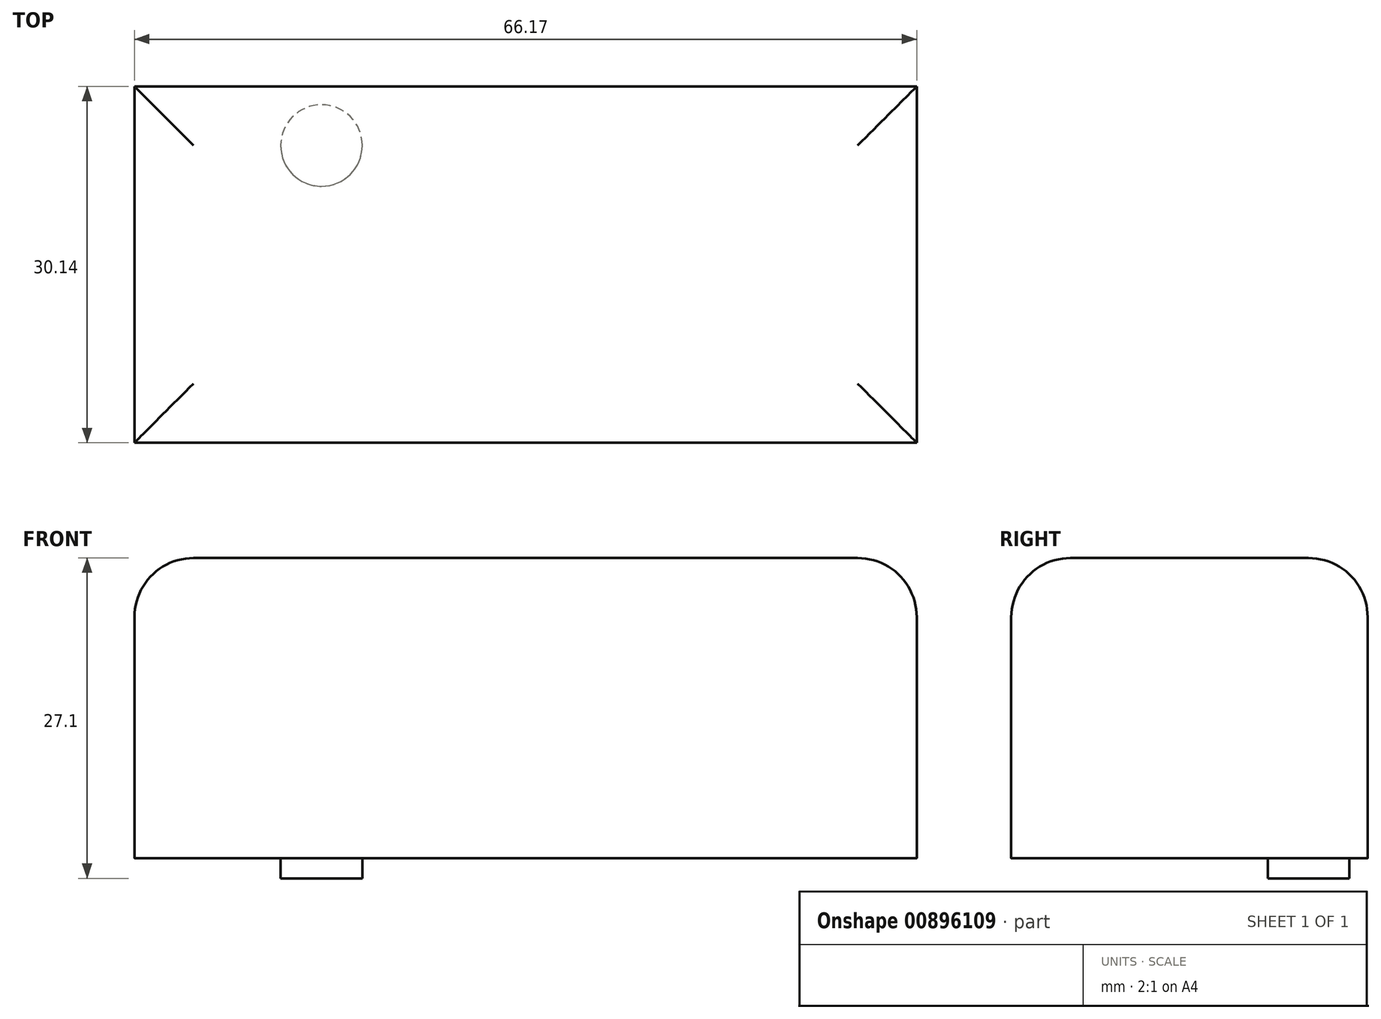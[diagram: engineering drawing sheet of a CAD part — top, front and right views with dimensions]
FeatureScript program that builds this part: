
annotation { "Feature Type Name" : "Feature", "Feature Type Description" : "" }
export const myFeature = defineFeature(function(context is Context, id is Id, definition is map)
    precondition{}
    {
        {
            var Q0;
            Q0=qCreatedBy(makeId("Top.planeOp"),FACE);
            var sketch = newSketch(context, id + "F0", { "sketchPlane" : qUnion([Q0])});
            skLineSegment(sketch, "E0.bottom", {"start": v(-31.19, 11.28) * mm, "end": v(34.98, 11.28) * mm});
            skLineSegment(sketch, "E0.top", {"start": v(-31.19, -18.86) * mm, "end": v(34.98, -18.86) * mm});
            skLineSegment(sketch, "E0.left", {"start": v(-31.19, 11.28) * mm, "end": v(-31.19, -18.86) * mm});
            skLineSegment(sketch, "E0.right", {"start": v(34.98, 11.28) * mm, "end": v(34.98, -18.86) * mm});
            skSolve(sketch);
        }
        {
            var Q0;
            Q0=makeQuery(id+"F0.imprint","IMPRINT",FACE,{"disambiguationData":[TD([[makeQuery(id+"F0.imprint","IMPRINT",EDGE,{"derivedFrom":sQuery(id+"F0.wireOp",EDGE,"E0.bottom")}),-1.0]])]});
            extrude(context, id + "F1", {"entities" : qUnion([Q0]), "depth" : 25.4 * mm, "offsetDistance" : 25.4 * mm});
        }
        {
            var Q0;
            Q0=qCreatedBy(makeId("Top.planeOp"),FACE);
            var sketch = newSketch(context, id + "F2", { "sketchPlane" : qUnion([Q0])});
            skCircle(sketch, "E1", {"center": v(21, -4.39) * mm, "radius": 10.1 * mm});
            skSolve(sketch);
        }
        {
            var Q0;
            Q0=sQuery(id+"F2.wireOp",EDGE,"E1");
            extrude(context, id + "F3", {"bodyType" : ToolBodyType.SURFACE, "surfaceEntities" : qUnion([Q0]), "depth" : 42.8 * mm, "offsetDistance" : 25 * mm});
        }
        {
            var Q0;
            Q0=makeQuery(id+"F1.opExtrude","SWEPT_FACE",FACE,{"disambiguationData":[OSD([sQuery(id+"F0.wireOp",EDGE,"E0.bottom")])]});
            var sketch = newSketch(context, id + "F4", { "sketchPlane" : qUnion([Q0])});
            skCircle(sketch, "E2", {"center": v(21.23, 13.84) * mm, "radius": 4.22 * mm});
            skSolve(sketch);
        }
        {
            var Q0;
            Q0=sQuery(id+"F4.wireOp",EDGE,"E2");
            extrude(context, id + "F5", {"bodyType" : ToolBodyType.SURFACE, "surfaceEntities" : qUnion([Q0]), "depth" : 3.1 * mm, "offsetDistance" : 25 * mm});
        }
        {
            var Q0;
            Q0=makeQuery(id+"F1.opExtrude","CAP_FACE",FACE,{"disambiguationData":[OSD([sQuery(id+"F0.wireOp",EDGE,"E0.bottom"),sQuery(id+"F0.wireOp",EDGE,"E0.top"),sQuery(id+"F0.wireOp",EDGE,"E0.left"),sQuery(id+"F0.wireOp",EDGE,"E0.right")])],"isStart":true});
            var sketch = newSketch(context, id + "F6", { "sketchPlane" : qUnion([Q0])});
            skCircle(sketch, "E3", {"center": v(-15.36, -6.28) * mm, "radius": 3.45 * mm});
            skSolve(sketch);
        }
        {
            var Q0;
            Q0 = qSketchRegion(id + "F6", true);
            extrude(context, id + "F7", {"entities" : qUnion([Q0]), "operationType" : NewBodyOperationType.ADD, "depth" : 1.7 * mm, "offsetDistance" : 25 * mm});
        }
        {
            var Q0;
            Q0=makeQuery(id+"F1.opExtrude","CAP_FACE",FACE,{"disambiguationData":[OSD([sQuery(id+"F0.wireOp",EDGE,"E0.bottom"),sQuery(id+"F0.wireOp",EDGE,"E0.top"),sQuery(id+"F0.wireOp",EDGE,"E0.left"),sQuery(id+"F0.wireOp",EDGE,"E0.right")])],"isStart":false});
            fillet(context, id + "F8", {"entities" : qUnion([Q0]), "radius" : 5 * mm, "tangentPropagation" : true, "allowEdgeOverflow" : false});
        }
        {
            var Q0;
            Q0=makeQuery(id+"F1.opExtrude","CAP_FACE",FACE,{"disambiguationData":[OSD([sQuery(id+"F0.wireOp",EDGE,"E0.bottom"),sQuery(id+"F0.wireOp",EDGE,"E0.top"),sQuery(id+"F0.wireOp",EDGE,"E0.left"),sQuery(id+"F0.wireOp",EDGE,"E0.right")])],"isStart":true});
            fillet(context, id + "F9", {"entities" : qUnion([Q0]), "radius" : 0.02 * mm, "tangentPropagation" : true, "allowEdgeOverflow" : false});
        }
    });
